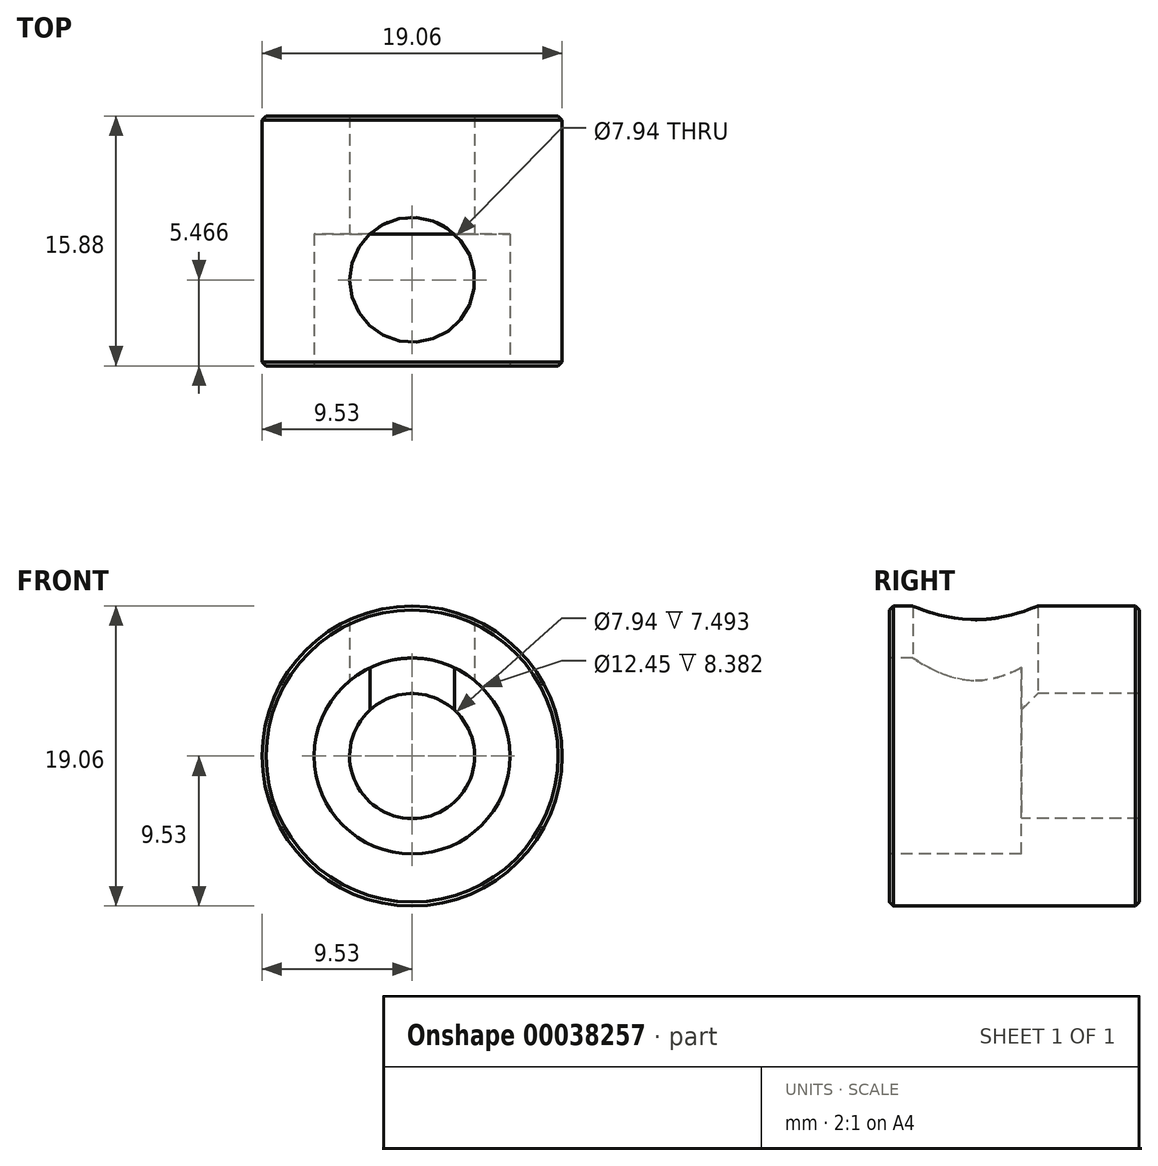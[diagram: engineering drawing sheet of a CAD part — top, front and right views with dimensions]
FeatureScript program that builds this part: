
annotation { "Feature Type Name" : "Feature", "Feature Type Description" : "" }
export const myFeature = defineFeature(function(context is Context, id is Id, definition is map)
    precondition{}
    {
        {
            var Q0;
            Q0=qCreatedBy(makeId("Front.planeOp"),FACE);
            var sketch = newSketch(context, id + "F0", { "sketchPlane" : qUnion([Q0])});
            skCircle(sketch, "E0", {"center": v(0, 0) * mm, "radius": 9.53 * mm});
            skSolve(sketch);
        }
        {
            var Q0;
            Q0=makeQuery(id+"F0.imprint","IMPRINT",FACE,{"disambiguationData":[TD([[makeQuery(id+"F0.imprint","IMPRINT",EDGE,{"derivedFrom":sQuery(id+"F0.wireOp",EDGE,"E0")}),1.0]])]});
            extrude(context, id + "F1", {"entities" : qUnion([Q0]), "depth" : 15.88 * mm});
        }
        {
            var Q0;
            Q0=makeQuery(id+"F1.opExtrude","CAP_FACE",FACE,{"disambiguationData":[OSD([sQuery(id+"F0.wireOp",EDGE,"E0")])],"isStart":false});
            var sketch = newSketch(context, id + "F2", { "sketchPlane" : qUnion([Q0])});
            skCircle(sketch, "E1", {"center": v(0, 0) * mm, "radius": 3.97 * mm});
            skSolve(sketch);
        }
        {
            var Q0;
            Q0 = qSketchRegion(id + "F2", true);
            extrude(context, id + "F3", {"entities" : qUnion([Q0]), "operationType" : NewBodyOperationType.REMOVE, "endBound" : BoundingType.THROUGH_ALL, "oppositeDirection" : true, "depth" : 25.4 * mm});
        }
        {
            var Q0;
            Q0=makeQuery(id+"F1.opExtrude","CAP_FACE",FACE,{"disambiguationData":[OSD([sQuery(id+"F0.wireOp",EDGE,"E0")])],"isStart":false});
            var sketch = newSketch(context, id + "F4", { "sketchPlane" : qUnion([Q0])});
            skCircle(sketch, "E2", {"center": v(0, 0) * mm, "radius": 6.22 * mm});
            skSolve(sketch);
        }
        {
            var Q0;
            Q0=makeQuery(id+"F4.imprint","IMPRINT",FACE,{"disambiguationData":[TD([[makeQuery(id+"F4.imprint","IMPRINT",EDGE,{"derivedFrom":sQuery(id+"F4.wireOp",EDGE,"E2")}),1.0]])]});
            extrude(context, id + "F5", {"entities" : qUnion([Q0]), "operationType" : NewBodyOperationType.REMOVE, "oppositeDirection" : true, "depth" : 8.38 * mm});
        }
        {
            var Q0;
            Q0=makeQuery(id+"F1.opExtrude","CAP_EDGE",EDGE,{"disambiguationData":[OSD([sQuery(id+"F0.wireOp",EDGE,"E0")])],"isStart":false});
            var Q1;
            Q1=makeQuery(id+"F1.opExtrude","CAP_EDGE",EDGE,{"disambiguationData":[OSD([sQuery(id+"F0.wireOp",EDGE,"E0")])],"isStart":true});
            chamfer(context, id + "F6", {"entities" : qUnion([Q0, Q1]), "width" : 0.25 * mm, "tangentPropagation" : true});
        }
        {
            var Q0;
            Q0=qCreatedBy(makeId("Top.planeOp"),FACE);
            var sketch = newSketch(context, id + "F7", { "sketchPlane" : qUnion([Q0])});
            skLineSegment(sketch, "E3", {"start": v(0, 0) * mm, "end": v(0, -18.15) * mm, "construction": true});
            skPoint(sketch, "E4", {"position": v(0, -10.41) * mm});
            skCircle(sketch, "E5", {"center": v(0, -10.41) * mm, "radius": 3.97 * mm});
            skSolve(sketch);
        }
        {
            var Q0;
            Q0=makeQuery(id+"F7.imprint","IMPRINT",FACE,{"disambiguationData":[TD([[makeQuery(id+"F7.imprint","IMPRINT",EDGE,{"derivedFrom":sQuery(id+"F7.wireOp",EDGE,"E5")}),1.0]])]});
            var Q1;
            Q1=makeQuery(id+"F1.opExtrude","SWEPT_FACE",FACE,{"disambiguationData":[OSD([sQuery(id+"F0.wireOp",EDGE,"E0")])]});
            extrude(context, id + "F8", {"entities" : qUnion([Q0]), "operationType" : NewBodyOperationType.REMOVE, "endBound" : BoundingType.UP_TO_SURFACE, "endBoundEntityFace" : qUnion([Q1]), "depth" : 25.4 * mm});
        }
    });
